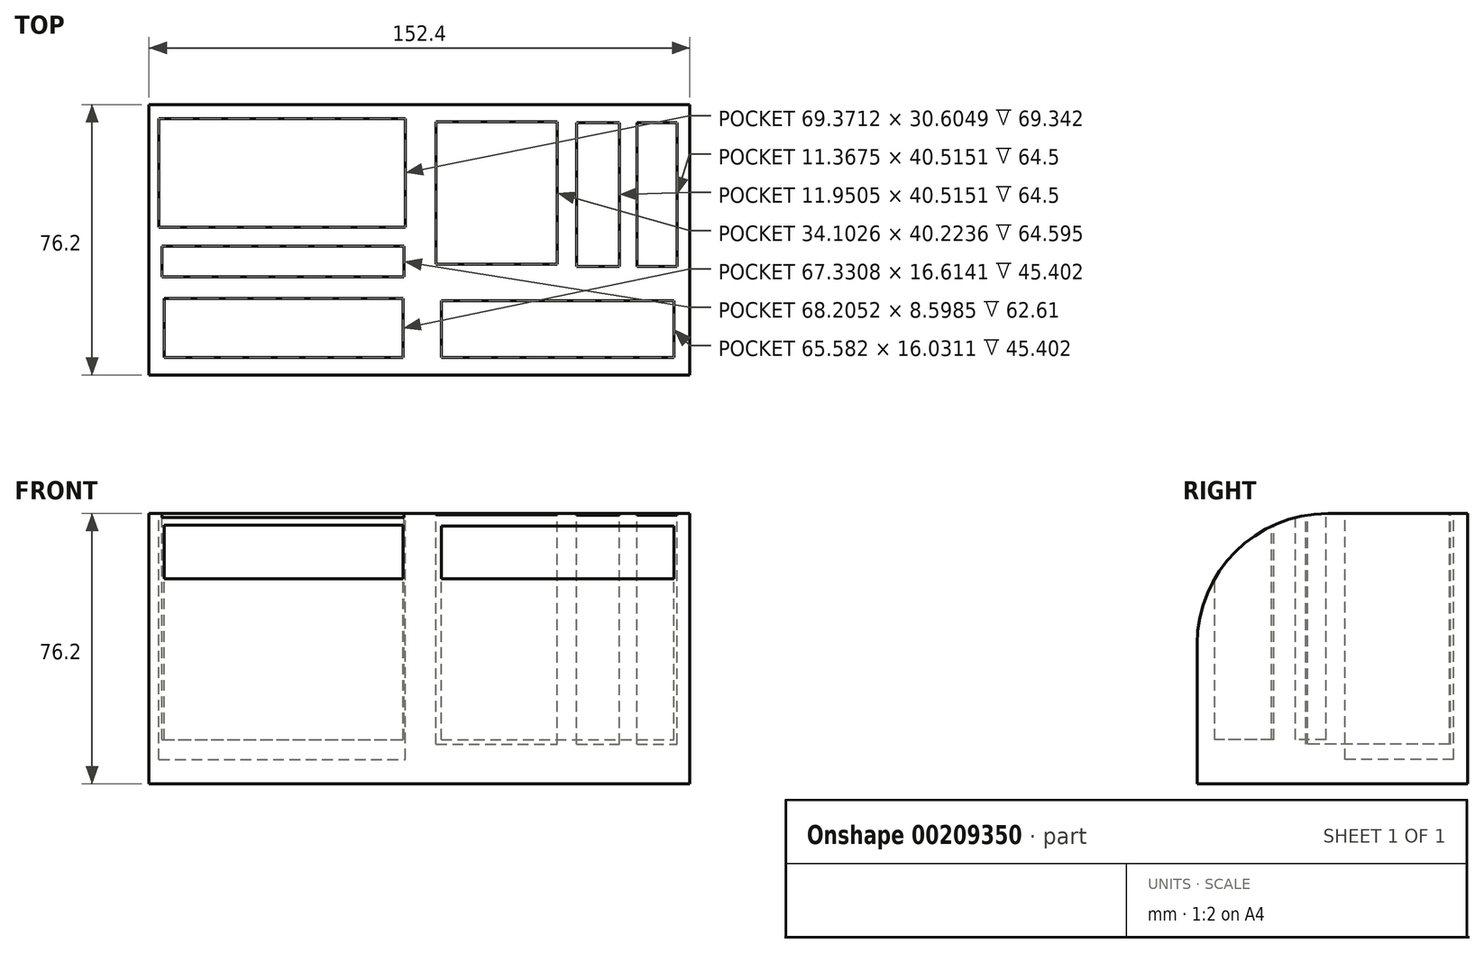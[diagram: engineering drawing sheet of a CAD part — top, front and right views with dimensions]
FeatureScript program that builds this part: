
annotation { "Feature Type Name" : "Feature", "Feature Type Description" : "" }
export const myFeature = defineFeature(function(context is Context, id is Id, definition is map)
    precondition{}
    {
        {
            var Q0;
            Q0=qCreatedBy(makeId("Top.planeOp"),FACE);
            var sketch = newSketch(context, id + "F0", { "sketchPlane" : qUnion([Q0])});
            skLineSegment(sketch, "E0.bottom", {"start": v(-76.32, 39.91) * mm, "end": v(76.08, 39.91) * mm});
            skLineSegment(sketch, "E0.top", {"start": v(-76.32, -36.29) * mm, "end": v(76.08, -36.29) * mm});
            skLineSegment(sketch, "E0.left", {"start": v(-76.32, 39.91) * mm, "end": v(-76.32, -36.29) * mm});
            skLineSegment(sketch, "E0.right", {"start": v(76.08, 39.91) * mm, "end": v(76.08, -36.29) * mm});
            skSolve(sketch);
        }
        {
            var Q0;
            Q0=makeQuery(id+"F0.imprint","IMPRINT",FACE,{"disambiguationData":[TD([[makeQuery(id+"F0.imprint","IMPRINT",EDGE,{"derivedFrom":sQuery(id+"F0.wireOp",EDGE,"E0.bottom")}),-1.0]])]});
            extrude(context, id + "F1", {"entities" : qUnion([Q0]), "depth" : 76.2 * mm});
        }
        {
            var Q0;
            Q0=makeQuery(id+"F1.opExtrude","CAP_EDGE",EDGE,{"disambiguationData":[OSD([sQuery(id+"F0.wireOp",EDGE,"E0.top")])],"isStart":false});
            fillet(context, id + "F2", {"entities" : qUnion([Q0]), "radius" : 36.8 * mm, "tangentPropagation" : true, "allowEdgeOverflow" : false});
        }
        {
            var Q0;
            Q0=makeQuery(id+"F1.opExtrude","CAP_FACE",FACE,{"disambiguationData":[OSD([sQuery(id+"F0.wireOp",EDGE,"E0.bottom"),sQuery(id+"F0.wireOp",EDGE,"E0.top"),sQuery(id+"F0.wireOp",EDGE,"E0.left"),sQuery(id+"F0.wireOp",EDGE,"E0.right")])],"isStart":false});
            var sketch = newSketch(context, id + "F3", { "sketchPlane" : qUnion([Q0])});
            skLineSegment(sketch, "E1.bottom", {"start": v(-73.51, 36) * mm, "end": v(-4.14, 36) * mm});
            skLineSegment(sketch, "E1.top", {"start": v(-73.51, 5.4) * mm, "end": v(-4.14, 5.4) * mm});
            skLineSegment(sketch, "E1.left", {"start": v(-73.51, 36) * mm, "end": v(-73.51, 5.4) * mm});
            skLineSegment(sketch, "E1.right", {"start": v(-4.14, 36) * mm, "end": v(-4.14, 5.4) * mm});
            skSolve(sketch);
        }
        {
            var Q0;
            Q0=makeQuery(id+"F3.imprint","IMPRINT",FACE,{"disambiguationData":[TD([[makeQuery(id+"F3.imprint","IMPRINT",EDGE,{"derivedFrom":sQuery(id+"F3.wireOp",EDGE,"E1.bottom")}),-1.0]])]});
            extrude(context, id + "F4", {"entities" : qUnion([Q0]), "operationType" : NewBodyOperationType.REMOVE, "oppositeDirection" : true, "depth" : 69.34 * mm});
        }
        {
            var Q0;
            Q0=makeQuery(id+"F1.opExtrude","CAP_FACE",FACE,{"disambiguationData":[OSD([sQuery(id+"F0.wireOp",EDGE,"E0.bottom"),sQuery(id+"F0.wireOp",EDGE,"E0.top"),sQuery(id+"F0.wireOp",EDGE,"E0.left"),sQuery(id+"F0.wireOp",EDGE,"E0.right")])],"isStart":false});
            var sketch = newSketch(context, id + "F5", { "sketchPlane" : qUnion([Q0])});
            skLineSegment(sketch, "E2.bottom", {"start": v(4.6, 35.12) * mm, "end": v(38.7, 35.12) * mm});
            skLineSegment(sketch, "E2.top", {"start": v(4.6, -5.1) * mm, "end": v(38.7, -5.1) * mm});
            skLineSegment(sketch, "E2.left", {"start": v(4.6, 35.12) * mm, "end": v(4.6, -5.1) * mm});
            skLineSegment(sketch, "E2.right", {"start": v(38.7, 35.12) * mm, "end": v(38.7, -5.1) * mm});
            skLineSegment(sketch, "E3.bottom", {"start": v(44.24, 34.83) * mm, "end": v(56.2, 34.83) * mm});
            skLineSegment(sketch, "E3.top", {"start": v(44.24, -5.68) * mm, "end": v(56.2, -5.68) * mm});
            skLineSegment(sketch, "E3.left", {"start": v(44.24, 34.83) * mm, "end": v(44.24, -5.68) * mm});
            skLineSegment(sketch, "E3.right", {"start": v(56.2, 34.83) * mm, "end": v(56.2, -5.68) * mm});
            skLineSegment(sketch, "E4.bottom", {"start": v(61.15, 34.83) * mm, "end": v(72.51, 34.83) * mm});
            skLineSegment(sketch, "E4.top", {"start": v(61.15, -5.68) * mm, "end": v(72.51, -5.68) * mm});
            skLineSegment(sketch, "E4.left", {"start": v(61.15, 34.83) * mm, "end": v(61.15, -5.68) * mm});
            skLineSegment(sketch, "E4.right", {"start": v(72.51, 34.83) * mm, "end": v(72.51, -5.68) * mm});
            skSolve(sketch);
        }
        {
            var Q0;
            {var subQ0=sQuery(id+"F5.wireOp",EDGE,"E2.bottom");Q0=makeQuery(id+"F5.imprint","IMPRINT",FACE,{"disambiguationData":[TD([[makeQuery(id+"F5.imprint","IMPRINT",EDGE,{"derivedFrom":subQ0}),-1.0]])]});}
            var Q1;
            {var subQ0=sQuery(id+"F5.wireOp",EDGE,"E2.top");Q1=makeQuery(id+"F5.imprint","IMPRINT",FACE,{"disambiguationData":[TD([[makeQuery(id+"F5.imprint","IMPRINT",EDGE,{"derivedFrom":subQ0}),1.0]])]});}
            var Q2;
            {var subQ0=sQuery(id+"F5.wireOp",EDGE,"E3.bottom");Q2=makeQuery(id+"F5.imprint","IMPRINT",FACE,{"disambiguationData":[TD([[makeQuery(id+"F5.imprint","IMPRINT",EDGE,{"derivedFrom":subQ0}),-1.0]])]});}
            var Q3;
            {var subQ0=sQuery(id+"F5.wireOp",EDGE,"E3.top");Q3=makeQuery(id+"F5.imprint","IMPRINT",FACE,{"disambiguationData":[TD([[makeQuery(id+"F5.imprint","IMPRINT",EDGE,{"derivedFrom":subQ0}),1.0]])]});}
            var Q4;
            {var subQ0=sQuery(id+"F5.wireOp",EDGE,"E4.bottom");Q4=makeQuery(id+"F5.imprint","IMPRINT",FACE,{"disambiguationData":[TD([[makeQuery(id+"F5.imprint","IMPRINT",EDGE,{"derivedFrom":subQ0}),-1.0]])]});}
            var Q5;
            {var subQ0=sQuery(id+"F5.wireOp",EDGE,"E4.top");Q5=makeQuery(id+"F5.imprint","IMPRINT",FACE,{"disambiguationData":[TD([[makeQuery(id+"F5.imprint","IMPRINT",EDGE,{"derivedFrom":subQ0}),1.0]])]});}
            extrude(context, id + "F6", {"entities" : qUnion([Q0, Q1, Q2, Q3, Q4, Q5]), "operationType" : NewBodyOperationType.REMOVE, "oppositeDirection" : true, "depth" : 65.02 * mm});
        }
        {
            var Q0;
            Q0=qCreatedBy(makeId("Top.planeOp"),FACE);
            var sketch = newSketch(context, id + "F7", { "sketchPlane" : qUnion([Q0])});
            skLineSegment(sketch, "E5.bottom", {"start": v(-72.64, 0) * mm, "end": v(-4.43, 0) * mm});
            skLineSegment(sketch, "E5.top", {"start": v(-72.64, -8.6) * mm, "end": v(-4.43, -8.6) * mm});
            skLineSegment(sketch, "E5.left", {"start": v(-72.64, 0) * mm, "end": v(-72.64, -8.6) * mm});
            skLineSegment(sketch, "E5.right", {"start": v(-4.43, 0) * mm, "end": v(-4.43, -8.6) * mm});
            skLineSegment(sketch, "E6.bottom", {"start": v(-72.06, -14.72) * mm, "end": v(-4.73, -14.72) * mm});
            skLineSegment(sketch, "E6.top", {"start": v(-72.06, -31.33) * mm, "end": v(-4.73, -31.33) * mm});
            skLineSegment(sketch, "E6.left", {"start": v(-72.06, -14.72) * mm, "end": v(-72.06, -31.33) * mm});
            skLineSegment(sketch, "E6.right", {"start": v(-4.73, -14.72) * mm, "end": v(-4.73, -31.33) * mm});
            skLineSegment(sketch, "E7.bottom", {"start": v(6.06, -15.3) * mm, "end": v(71.64, -15.3) * mm});
            skLineSegment(sketch, "E7.top", {"start": v(6.06, -31.33) * mm, "end": v(71.64, -31.33) * mm});
            skLineSegment(sketch, "E7.left", {"start": v(6.06, -15.3) * mm, "end": v(6.06, -31.33) * mm});
            skLineSegment(sketch, "E7.right", {"start": v(71.64, -15.3) * mm, "end": v(71.64, -31.33) * mm});
            skSolve(sketch);
        }
        {
            var Q0;
            Q0=makeQuery(id+"F7.imprint","IMPRINT",FACE,{"disambiguationData":[TD([[makeQuery(id+"F7.imprint","IMPRINT",EDGE,{"derivedFrom":sQuery(id+"F7.wireOp",EDGE,"E7.bottom")}),-1.0]])]});
            extrude(context, id + "F8", {"entities" : qUnion([Q0]), "operationType" : NewBodyOperationType.ADD, "depth" : 83.82 * mm});
        }
        {
            var Q0;
            Q0=makeQuery(id+"F8.opExtrude","CAP_FACE",FACE,{"disambiguationData":[OSD([sQuery(id+"F7.wireOp",EDGE,"E7.bottom"),sQuery(id+"F7.wireOp",EDGE,"E7.top"),sQuery(id+"F7.wireOp",EDGE,"E7.left"),sQuery(id+"F7.wireOp",EDGE,"E7.right")])],"isStart":false});
            extrude(context, id + "F9", {"entities" : qUnion([Q0]), "operationType" : NewBodyOperationType.REMOVE, "oppositeDirection" : true, "depth" : 66.55 * mm});
        }
        {
            var Q0;
            Q0 = qSketchRegion(id + "F7", true);
            extrude(context, id + "F10", {"entities" : qUnion([Q0]), "operationType" : NewBodyOperationType.ADD, "depth" : 100.08 * mm});
        }
        {
            var Q0;
            Q0=makeQuery(id+"F10.opExtrude","CAP_FACE",FACE,{"disambiguationData":[OSD([sQuery(id+"F7.wireOp",EDGE,"E6.bottom"),sQuery(id+"F7.wireOp",EDGE,"E6.top"),sQuery(id+"F7.wireOp",EDGE,"E6.left"),sQuery(id+"F7.wireOp",EDGE,"E6.right")])],"isStart":false});
            var Q1;
            Q1=makeQuery(id+"F10.opExtrude","CAP_FACE",FACE,{"disambiguationData":[OSD([sQuery(id+"F7.wireOp",EDGE,"E5.bottom"),sQuery(id+"F7.wireOp",EDGE,"E5.top"),sQuery(id+"F7.wireOp",EDGE,"E5.left"),sQuery(id+"F7.wireOp",EDGE,"E5.right")])],"isStart":false});
            var Q2;
            Q2=makeQuery(id+"F10.opExtrude","CAP_FACE",FACE,{"disambiguationData":[OSD([sQuery(id+"F7.wireOp",EDGE,"E7.bottom"),sQuery(id+"F7.wireOp",EDGE,"E7.top"),sQuery(id+"F7.wireOp",EDGE,"E7.left"),sQuery(id+"F7.wireOp",EDGE,"E7.right")])],"isStart":false});
            extrude(context, id + "F11", {"entities" : qUnion([Q0, Q1, Q2]), "operationType" : NewBodyOperationType.REMOVE, "oppositeDirection" : true, "depth" : 87.63 * mm});
        }
    });
